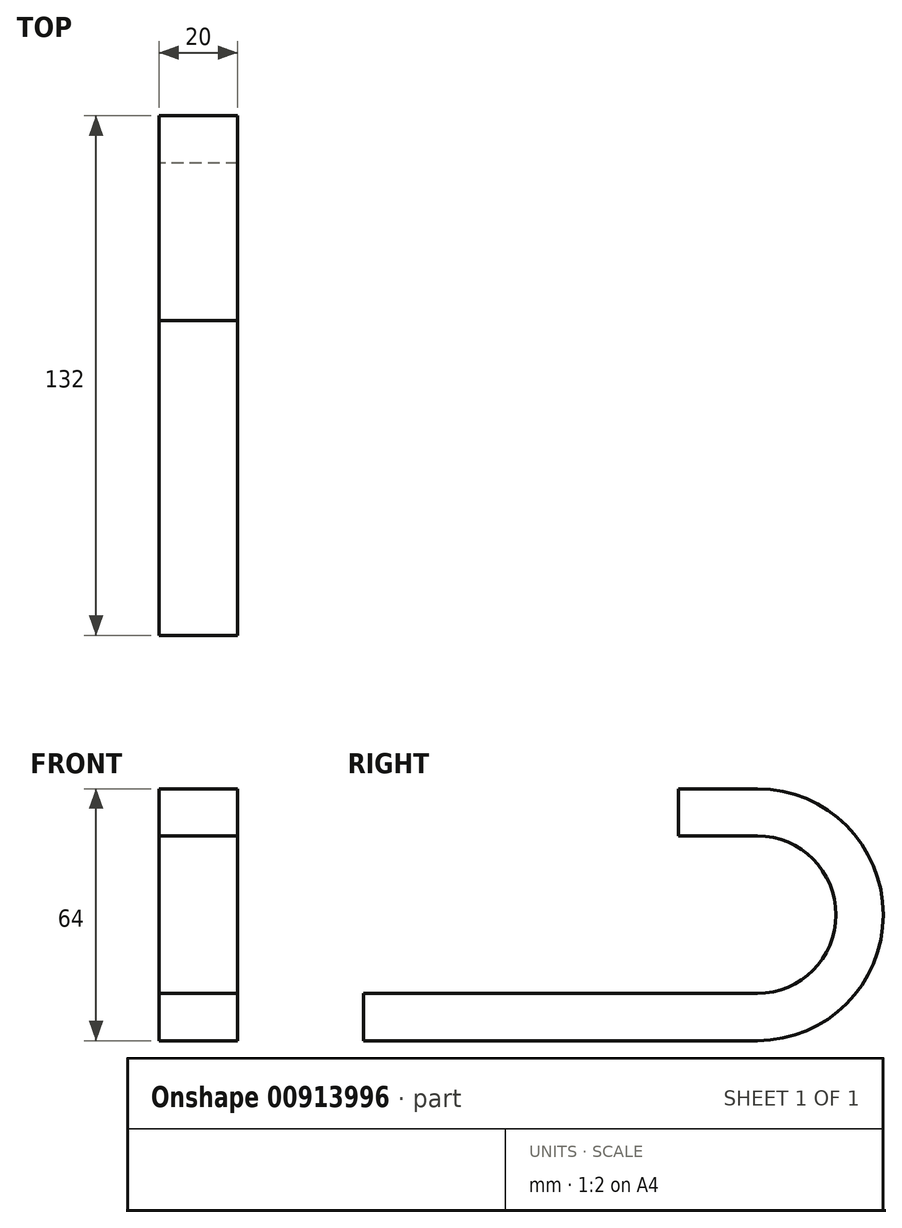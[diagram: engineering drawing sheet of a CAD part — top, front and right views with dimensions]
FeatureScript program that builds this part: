
annotation { "Feature Type Name" : "Feature", "Feature Type Description" : "" }
export const myFeature = defineFeature(function(context is Context, id is Id, definition is map)
    precondition{}
    {
        {
            var Q0;
            Q0=qCreatedBy(makeId("Right.planeOp"),FACE);
            var sketch = newSketch(context, id + "F0", { "sketchPlane" : qUnion([Q0])});
            skLineSegment(sketch, "E0", {"start": v(0, 0) * mm, "end": v(100, 0) * mm});
            skArc(sketch, "E1", {"start": v(100, 0) * mm, "mid": v(120, 20) * mm, "end": v(100, 40) * mm});
            skArc(sketch, "E2", {"start": v(100, -12) * mm, "mid": v(132, 20) * mm, "end": v(100, 52) * mm});
            skLineSegment(sketch, "E3", {"start": v(100, -12) * mm, "end": v(0, -12) * mm});
            skLineSegment(sketch, "E4", {"start": v(0, -12) * mm, "end": v(0, 0) * mm});
            skLineSegment(sketch, "E5", {"start": v(100, 40) * mm, "end": v(80, 40) * mm});
            skLineSegment(sketch, "E6", {"start": v(80, 40) * mm, "end": v(80, 52) * mm});
            skLineSegment(sketch, "E7", {"start": v(80, 52) * mm, "end": v(100, 52) * mm});
            skSolve(sketch);
        }
        {
            var Q0;
            Q0 = qSketchRegion(id + "F0", true);
            extrude(context, id + "F1", {"entities" : qUnion([Q0]), "depth" : 20 * mm, "offsetDistance" : 25 * mm});
        }
    });
